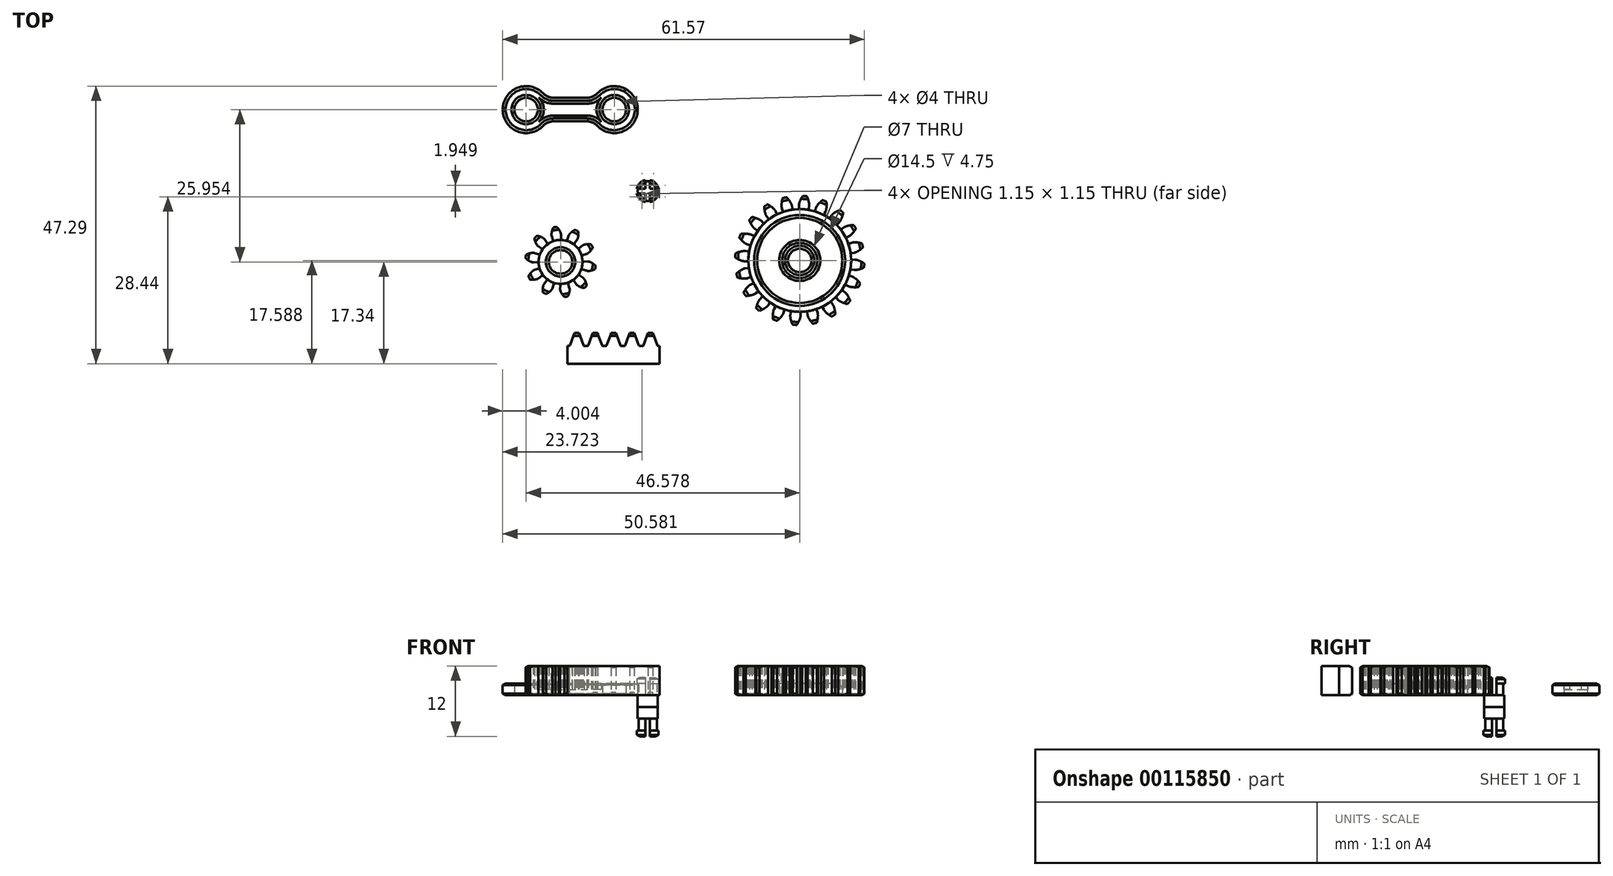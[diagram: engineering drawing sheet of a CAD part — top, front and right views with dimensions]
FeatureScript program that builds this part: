
annotation { "Feature Type Name" : "Feature", "Feature Type Description" : "" }
export const myFeature = defineFeature(function(context is Context, id is Id, definition is map)
    precondition{}
    {
        {
            var Q0;
            Q0=qCreatedBy(makeId("Top.planeOp"),FACE);
            var sketch = newSketch(context, id + "F0", { "sketchPlane" : qUnion([Q0])});
            skArc(sketch, "E0", {"start": v(4.77, -1.23) * mm, "mid": v(4.82, -0.94) * mm, "end": v(4.86, -0.65) * mm});
            skFitSpline(sketch, "E1", {"points": [v(3.6, 0.07) * mm, v(3.6, 0.07) * mm, v(3.6, 0.07) * mm, v(3.6, 0.07) * mm, v(3.6, 0.07) * mm, v(3.6, 0.07) * mm, v(3.6, 0.07) * mm, v(3.62, 0.07) * mm, v(3.63, 0.07) * mm, v(3.64, 0.07) * mm, v(3.65, 0.06) * mm, v(3.66, 0.06) * mm, v(3.68, 0.06) * mm, v(3.7, 0.06) * mm, v(3.71, 0.05) * mm, v(3.73, 0.05) * mm, v(3.75, 0.04) * mm, v(3.77, 0.04) * mm, v(3.8, 0.03) * mm, v(3.82, 0.03) * mm, v(3.84, 0.02) * mm, v(3.87, 0) * mm, v(3.9, 0) * mm, v(3.93, -0.01) * mm, v(3.96, -0.02) * mm, v(3.99, -0.04) * mm, v(4.02, -0.05) * mm, v(4.05, -0.07) * mm, v(4.09, -0.08) * mm, v(4.12, -0.1) * mm, v(4.16, -0.12) * mm, v(4.2, -0.14) * mm, v(4.23, -0.16) * mm, v(4.27, -0.18) * mm, v(4.31, -0.2) * mm, v(4.35, -0.23) * mm, v(4.4, -0.26) * mm, v(4.43, -0.3) * mm, v(4.48, -0.32) * mm, v(4.52, -0.35) * mm, v(4.56, -0.39) * mm, v(4.6, -0.42) * mm, v(4.65, -0.46) * mm, v(4.7, -0.5) * mm, v(4.74, -0.54) * mm, v(4.79, -0.58) * mm, v(4.83, -0.62) * mm, v(4.85, -0.64) * mm, v(4.86, -0.65) * mm]});
            skFitSpline(sketch, "E2", {"points": [v(3.34, -1.52) * mm, v(3.34, -1.52) * mm, v(3.34, -1.52) * mm, v(3.34, -1.52) * mm, v(3.35, -1.52) * mm, v(3.35, -1.52) * mm, v(3.36, -1.52) * mm, v(3.36, -1.53) * mm, v(3.37, -1.53) * mm, v(3.38, -1.53) * mm, v(3.4, -1.53) * mm, v(3.4, -1.53) * mm, v(3.42, -1.54) * mm, v(3.44, -1.54) * mm, v(3.46, -1.54) * mm, v(3.48, -1.54) * mm, v(3.5, -1.54) * mm, v(3.52, -1.54) * mm, v(3.54, -1.55) * mm, v(3.57, -1.55) * mm, v(3.6, -1.55) * mm, v(3.62, -1.55) * mm, v(3.65, -1.54) * mm, v(3.68, -1.54) * mm, v(3.72, -1.54) * mm, v(3.75, -1.54) * mm, v(3.78, -1.54) * mm, v(3.82, -1.53) * mm, v(3.86, -1.53) * mm, v(3.9, -1.52) * mm, v(3.94, -1.51) * mm, v(3.98, -1.5) * mm, v(4.02, -1.5) * mm, v(4.07, -1.49) * mm, v(4.11, -1.48) * mm, v(4.16, -1.46) * mm, v(4.2, -1.45) * mm, v(4.25, -1.44) * mm, v(4.3, -1.42) * mm, v(4.35, -1.4) * mm, v(4.4, -1.38) * mm, v(4.46, -1.36) * mm, v(4.51, -1.34) * mm, v(4.57, -1.32) * mm, v(4.62, -1.3) * mm, v(4.68, -1.27) * mm, v(4.73, -1.25) * mm, v(4.76, -1.23) * mm, v(4.77, -1.23) * mm]});
            skLineSegment(sketch, "E3", {"start": v(3.6, 0.07) * mm, "end": v(2.88, 0.06) * mm});
            skLineSegment(sketch, "E4", {"start": v(2.67, -1.3) * mm, "end": v(3.34, -1.52) * mm});
            skArc(sketch, "E5", {"start": v(2.36, -1.43) * mm, "mid": v(-4.81, 0.59) * mm, "end": v(2.63, 0.3) * mm});
            skPoint(sketch, "E6.visualSharp", {"position": v(2.64, 0.06) * mm});
            skArc(sketch, "E6.filletArc", {"start": v(2.63, 0.3) * mm, "mid": v(2.71, 0.12) * mm, "end": v(2.88, 0.06) * mm});
            skPoint(sketch, "E7.visualSharp", {"position": v(2.44, -1.21) * mm});
            skArc(sketch, "E7.filletArc", {"start": v(2.67, -1.3) * mm, "mid": v(2.49, -1.3) * mm, "end": v(2.36, -1.43) * mm});
            skCircle(sketch, "E8", {"center": v(-1.1, 0) * mm, "radius": 2 * mm});
            skCircle(sketch, "E9", {"center": v(-1.1, 0) * mm, "radius": 3.75 * mm});
            skSolve(sketch);
        }
        {
            var Q0;
            Q0=makeQuery(id+"F0.imprint","IMPRINT",FACE,{"disambiguationData":[TD([[makeQuery(id+"F0.imprint","IMPRINT",EDGE,{"derivedFrom":sQuery(id+"F0.wireOp",EDGE,"E0")}),1.0]])]});
            extrude(context, id + "F1", {"entities" : qUnion([Q0]), "depth" : 5 * mm});
        }
        {
            var Q0;
            Q0=makeQuery(id+"F1.opExtrude","CAP_EDGE",EDGE,{"disambiguationData":[OSD([sQuery(id+"F0.wireOp",EDGE,"E0")])],"isStart":false});
            var Q1;
            Q1=makeQuery(id+"F1.opExtrude","CAP_EDGE",EDGE,{"disambiguationData":[OSD([sQuery(id+"F0.wireOp",EDGE,"E0")])],"isStart":true});
            chamfer(context, id + "F2", {"entities" : qUnion([Q0, Q1]), "chamferType" : ChamferType.TWO_OFFSETS, "width1" : .5 * mm, "oppositeDirection" : false, "width2" : .25 * mm, "tangentPropagation" : true});
        }
        {
            var Q0;
            Q0=makeQuery(id+"F1.opExtrude","SWEPT_BODY",BODY,{"disambiguationData":[OSD([sQuery(id+"F0.wireOp",EDGE,"E0"),sQuery(id+"F0.wireOp",EDGE,"E1"),sQuery(id+"F0.wireOp",EDGE,"E2"),sQuery(id+"F0.wireOp",EDGE,"E3"),sQuery(id+"F0.wireOp",EDGE,"E4"),sQuery(id+"F0.wireOp",EDGE,"E6.filletArc"),sQuery(id+"F0.wireOp",EDGE,"E7.filletArc"),sQuery(id+"F0.wireOp",EDGE,"E9")])]});
            var Q1;
            Q1=sQuery(id+"F0.wireOp",EDGE,"E8");
            circularPattern(context, id + "F3", {"entities" : qUnion([Q0]), "axis" : qUnion([Q1]), "angle" : 36 * degree, "instanceCount" : 10});
        }
        {
            var Q0;
            Q0=makeQuery(id+"F0.imprint","IMPRINT",FACE,{"disambiguationData":[TD([[makeQuery(id+"F0.imprint","IMPRINT",EDGE,{"derivedFrom":sQuery(id+"F0.wireOp",EDGE,"E8")}),-1.0]])]});
            extrude(context, id + "F4", {"entities" : qUnion([Q0]), "depth" : 5 * mm});
        }
        {
            var Q0;
            Q0=makeQuery(id+"F4.opExtrude","CAP_EDGE",EDGE,{"disambiguationData":[OSD([sQuery(id+"F0.wireOp",EDGE,"E8")])],"isStart":false});
            var Q1;
            Q1=makeQuery(id+"F4.opExtrude","CAP_EDGE",EDGE,{"disambiguationData":[OSD([sQuery(id+"F0.wireOp",EDGE,"E8")])],"isStart":true});
            chamfer(context, id + "F5", {"entities" : qUnion([Q0, Q1]), "chamferType" : ChamferType.TWO_OFFSETS, "width1" : .25 * mm, "oppositeDirection" : false, "width2" : .5 * mm, "tangentPropagation" : true});
        }
        {
            var Q0;
            Q0=qCreatedBy(makeId("Top.planeOp"),FACE);
            var sketch = newSketch(context, id + "F6", { "sketchPlane" : qUnion([Q0])});
            skArc(sketch, "E10", {"start": v(50.54, -0.96) * mm, "mid": v(50.58, -0.62) * mm, "end": v(50.6, -0.27) * mm});
            skFitSpline(sketch, "E11", {"points": [v(49, 0.39) * mm, v(49, 0.39) * mm, v(49, 0.39) * mm, v(49.01, 0.39) * mm, v(49.02, 0.39) * mm, v(49.03, 0.39) * mm, v(49.04, 0.39) * mm, v(49.06, 0.39) * mm, v(49.08, 0.38) * mm, v(49.1, 0.38) * mm, v(49.12, 0.38) * mm, v(49.15, 0.37) * mm, v(49.18, 0.37) * mm, v(49.21, 0.36) * mm, v(49.25, 0.36) * mm, v(49.29, 0.35) * mm, v(49.33, 0.34) * mm, v(49.37, 0.33) * mm, v(49.41, 0.31) * mm, v(49.46, 0.3) * mm, v(49.51, 0.28) * mm, v(49.57, 0.26) * mm, v(49.62, 0.24) * mm, v(49.68, 0.22) * mm, v(49.74, 0.2) * mm, v(49.8, 0.17) * mm, v(49.86, 0.15) * mm, v(49.93, 0.11) * mm, v(50, 0.08) * mm, v(50.07, 0.05) * mm, v(50.14, 0) * mm, v(50.22, -0.03) * mm, v(50.3, -0.07) * mm, v(50.37, -0.12) * mm, v(50.45, -0.17) * mm, v(50.53, -0.22) * mm, v(50.58, -0.25) * mm, v(50.6, -0.27) * mm]});
            skFitSpline(sketch, "E12", {"points": [v(48.87, -1.36) * mm, v(48.87, -1.36) * mm, v(48.87, -1.36) * mm, v(48.88, -1.36) * mm, v(48.88, -1.36) * mm, v(48.9, -1.36) * mm, v(48.9, -1.36) * mm, v(48.92, -1.37) * mm, v(48.94, -1.37) * mm, v(48.96, -1.37) * mm, v(48.99, -1.37) * mm, v(49.01, -1.37) * mm, v(49.04, -1.37) * mm, v(49.08, -1.37) * mm, v(49.11, -1.37) * mm, v(49.15, -1.36) * mm, v(49.2, -1.36) * mm, v(49.24, -1.36) * mm, v(49.28, -1.35) * mm, v(49.33, -1.34) * mm, v(49.39, -1.33) * mm, v(49.44, -1.33) * mm, v(49.5, -1.31) * mm, v(49.56, -1.3) * mm, v(49.62, -1.29) * mm, v(49.69, -1.27) * mm, v(49.75, -1.25) * mm, v(49.82, -1.23) * mm, v(49.9, -1.21) * mm, v(49.97, -1.19) * mm, v(50.05, -1.16) * mm, v(50.13, -1.13) * mm, v(50.21, -1.1) * mm, v(50.3, -1.07) * mm, v(50.38, -1.03) * mm, v(50.46, -1) * mm, v(50.52, -0.97) * mm, v(50.54, -0.96) * mm]});
            skLineSegment(sketch, "E13", {"start": v(49, 0.39) * mm, "end": v(48.6, 0.38) * mm});
            skLineSegment(sketch, "E14", {"start": v(48.48, -1.3) * mm, "end": v(48.87, -1.36) * mm});
            skArc(sketch, "E15", {"start": v(48.19, -1.49) * mm, "mid": v(30.89, 0.93) * mm, "end": v(48.35, 0.62) * mm});
            skPoint(sketch, "E16.visualSharp", {"position": v(48.36, 0.38) * mm});
            skArc(sketch, "E16.filletArc", {"start": v(48.35, 0.62) * mm, "mid": v(48.43, 0.45) * mm, "end": v(48.6, 0.38) * mm});
            skPoint(sketch, "E17.visualSharp", {"position": v(48.23, -1.25) * mm});
            skArc(sketch, "E17.filletArc", {"start": v(48.48, -1.3) * mm, "mid": v(48.3, -1.33) * mm, "end": v(48.19, -1.49) * mm});
            skCircle(sketch, "E18", {"center": v(39.61, 0.25) * mm, "radius": 8.75 * mm});
            skCircle(sketch, "E19", {"center": v(39.61, 0.25) * mm, "radius": 2 * mm});
            skCircle(sketch, "E20", {"center": v(39.61, 0.25) * mm, "radius": 3.5 * mm});
            skCircle(sketch, "E21", {"center": v(39.61, 0.25) * mm, "radius": 7.25 * mm});
            skSolve(sketch);
        }
        {
            var Q0;
            Q0=makeQuery(id+"F6.imprint","IMPRINT",FACE,{"disambiguationData":[TD([[makeQuery(id+"F6.imprint","IMPRINT",EDGE,{"derivedFrom":sQuery(id+"F6.wireOp",EDGE,"E10")}),1.0]])]});
            extrude(context, id + "F7", {"entities" : qUnion([Q0]), "depth" : 5 * mm});
        }
        {
            var Q0;
            Q0=makeQuery(id+"F7.opExtrude","CAP_EDGE",EDGE,{"disambiguationData":[OSD([sQuery(id+"F6.wireOp",EDGE,"E10")])],"isStart":false});
            var Q1;
            Q1=makeQuery(id+"F7.opExtrude","CAP_EDGE",EDGE,{"disambiguationData":[OSD([sQuery(id+"F6.wireOp",EDGE,"E10")])],"isStart":true});
            chamfer(context, id + "F8", {"entities" : qUnion([Q0, Q1]), "chamferType" : ChamferType.TWO_OFFSETS, "width1" : .5 * mm, "oppositeDirection" : false, "width2" : .25 * mm, "tangentPropagation" : true});
        }
        {
            var Q0;
            Q0=makeQuery(id+"F7.opExtrude","SWEPT_BODY",BODY,{"disambiguationData":[OSD([sQuery(id+"F6.wireOp",EDGE,"E10"),sQuery(id+"F6.wireOp",EDGE,"E11"),sQuery(id+"F6.wireOp",EDGE,"E12"),sQuery(id+"F6.wireOp",EDGE,"E13"),sQuery(id+"F6.wireOp",EDGE,"E14"),sQuery(id+"F6.wireOp",EDGE,"E16.filletArc"),sQuery(id+"F6.wireOp",EDGE,"E17.filletArc"),sQuery(id+"F6.wireOp",EDGE,"E18")])]});
            var Q1;
            Q1=sQuery(id+"F6.wireOp",EDGE,"E19");
            circularPattern(context, id + "F9", {"entities" : qUnion([Q0]), "axis" : qUnion([Q1]), "angle" : 18 * degree, "instanceCount" : 20});
        }
        {
            var Q0;
            Q0=makeQuery(id+"F6.imprint","IMPRINT",FACE,{"disambiguationData":[TD([[makeQuery(id+"F6.imprint","IMPRINT",EDGE,{"derivedFrom":sQuery(id+"F6.wireOp",EDGE,"E21")}),-1.0]])]});
            var Q1;
            Q1=makeQuery(id+"F6.imprint","IMPRINT",FACE,{"disambiguationData":[TD([[makeQuery(id+"F6.imprint","IMPRINT",EDGE,{"derivedFrom":sQuery(id+"F6.wireOp",EDGE,"E19")}),-1.0]])]});
            extrude(context, id + "F10", {"entities" : qUnion([Q0, Q1]), "depth" : 5 * mm});
        }
        {
            var Q0;
            Q0=makeQuery(id+"F6.imprint","IMPRINT",FACE,{"disambiguationData":[TD([[makeQuery(id+"F6.imprint","IMPRINT",EDGE,{"derivedFrom":sQuery(id+"F6.wireOp",EDGE,"E20")}),-1.0]])]});
            extrude(context, id + "F11", {"entities" : qUnion([Q0]), "depth" : 2 * mm});
        }
        {
            var Q0;
            Q0=makeQuery(id+"F11.opExtrude","CAP_EDGE",EDGE,{"disambiguationData":[OSD([sQuery(id+"F6.wireOp",EDGE,"E21")])],"isStart":false});
            var Q1;
            Q1=makeQuery(id+"F11.opExtrude","CAP_EDGE",EDGE,{"disambiguationData":[OSD([sQuery(id+"F6.wireOp",EDGE,"E20")])],"isStart":false});
            fillet(context, id + "F12", {"entities" : qUnion([Q0, Q1]), "radius" : 1 * mm, "tangentPropagation" : true, "allowEdgeOverflow" : false});
        }
        {
            var Q0;
            Q0=makeQuery(id+"F10.opExtrude","CAP_EDGE",EDGE,{"disambiguationData":[OSD([sQuery(id+"F6.wireOp",EDGE,"E21")])],"isStart":false});
            var Q1;
            Q1=makeQuery(id+"F10.opExtrude","CAP_EDGE",EDGE,{"disambiguationData":[OSD([sQuery(id+"F6.wireOp",EDGE,"E19")])],"isStart":false});
            chamfer(context, id + "F13", {"entities" : qUnion([Q0, Q1]), "chamferType" : ChamferType.TWO_OFFSETS, "width1" : .25 * mm, "oppositeDirection" : false, "width2" : .5 * mm, "tangentPropagation" : true});
        }
        {
            var Q0;
            Q0=makeQuery(id+"F10.opExtrude","CAP_EDGE",EDGE,{"disambiguationData":[OSD([sQuery(id+"F6.wireOp",EDGE,"E20")])],"isStart":false});
            var Q1;
            Q1=makeQuery(id+"F10.opExtrude","CAP_EDGE",EDGE,{"disambiguationData":[OSD([sQuery(id+"F6.wireOp",EDGE,"E19")])],"isStart":true});
            chamfer(context, id + "F14", {"entities" : qUnion([Q0, Q1]), "chamferType" : ChamferType.TWO_OFFSETS, "width1" : .5 * mm, "oppositeDirection" : false, "width2" : .25 * mm, "tangentPropagation" : true});
        }
        {
            var Q0;
            Q0=qCreatedBy(makeId("Top.planeOp"),FACE);
            var sketch = newSketch(context, id + "F15", { "sketchPlane" : qUnion([Q0])});
            skLineSegment(sketch, "E22", {"start": v(0.48, -14.18) * mm, "end": v(1.24, -12.1) * mm});
            skLineSegment(sketch, "E23", {"start": v(1.24, -12.1) * mm, "end": v(2.04, -12.1) * mm});
            skLineSegment(sketch, "E24", {"start": v(2.04, -12.1) * mm, "end": v(2.8, -14.18) * mm});
            skLineSegment(sketch, "E25", {"start": v(3.03, -14.34) * mm, "end": v(3.38, -14.34) * mm});
            skLineSegment(sketch, "E26", {"start": v(3.62, -14.18) * mm, "end": v(4.38, -12.1) * mm});
            skLineSegment(sketch, "E27", {"start": v(4.38, -12.1) * mm, "end": v(5.18, -12.1) * mm});
            skLineSegment(sketch, "E28", {"start": v(5.18, -12.1) * mm, "end": v(5.94, -14.18) * mm});
            skLineSegment(sketch, "E29", {"start": v(6.17, -14.34) * mm, "end": v(6.53, -14.34) * mm});
            skLineSegment(sketch, "E30", {"start": v(6.76, -14.18) * mm, "end": v(7.52, -12.1) * mm});
            skLineSegment(sketch, "E31", {"start": v(7.52, -12.1) * mm, "end": v(8.32, -12.1) * mm});
            skLineSegment(sketch, "E32", {"start": v(8.32, -12.1) * mm, "end": v(9.08, -14.18) * mm});
            skLineSegment(sketch, "E33", {"start": v(9.31, -14.34) * mm, "end": v(9.67, -14.34) * mm});
            skLineSegment(sketch, "E34", {"start": v(9.9, -14.18) * mm, "end": v(10.66, -12.1) * mm});
            skLineSegment(sketch, "E35", {"start": v(10.66, -12.1) * mm, "end": v(11.46, -12.1) * mm});
            skLineSegment(sketch, "E36", {"start": v(11.46, -12.1) * mm, "end": v(12.22, -14.18) * mm});
            skLineSegment(sketch, "E37", {"start": v(12.46, -14.34) * mm, "end": v(12.8, -14.34) * mm});
            skLineSegment(sketch, "E38", {"start": v(13.04, -14.18) * mm, "end": v(13.8, -12.1) * mm});
            skLineSegment(sketch, "E39", {"start": v(13.8, -12.1) * mm, "end": v(14.6, -12.1) * mm});
            skLineSegment(sketch, "E40", {"start": v(14.6, -12.1) * mm, "end": v(15.36, -14.18) * mm});
            skLineSegment(sketch, "E41", {"start": v(0.07, -14.34) * mm, "end": v(0.07, -17.34) * mm});
            skLineSegment(sketch, "E42", {"start": v(15.77, -14.34) * mm, "end": v(15.77, -17.34) * mm});
            skLineSegment(sketch, "E43", {"start": v(0.07, -14.34) * mm, "end": v(0.24, -14.34) * mm});
            skLineSegment(sketch, "E44", {"start": v(0.07, -17.34) * mm, "end": v(15.77, -17.34) * mm});
            skLineSegment(sketch, "E45", {"start": v(15.6, -14.34) * mm, "end": v(15.77, -14.34) * mm});
            skPoint(sketch, "E46.visualSharp", {"position": v(0.42, -14.34) * mm});
            skArc(sketch, "E46.filletArc", {"start": v(0.24, -14.34) * mm, "mid": v(0.39, -14.3) * mm, "end": v(0.48, -14.18) * mm});
            skPoint(sketch, "E47.visualSharp", {"position": v(2.86, -14.34) * mm});
            skArc(sketch, "E47.filletArc", {"start": v(2.8, -14.18) * mm, "mid": v(2.89, -14.3) * mm, "end": v(3.03, -14.34) * mm});
            skPoint(sketch, "E48.visualSharp", {"position": v(3.56, -14.34) * mm});
            skArc(sketch, "E48.filletArc", {"start": v(3.38, -14.34) * mm, "mid": v(3.53, -14.3) * mm, "end": v(3.62, -14.18) * mm});
            skPoint(sketch, "E49.visualSharp", {"position": v(6, -14.34) * mm});
            skArc(sketch, "E49.filletArc", {"start": v(5.94, -14.18) * mm, "mid": v(6.03, -14.3) * mm, "end": v(6.17, -14.34) * mm});
            skPoint(sketch, "E50.visualSharp", {"position": v(6.7, -14.34) * mm});
            skArc(sketch, "E50.filletArc", {"start": v(6.53, -14.34) * mm, "mid": v(6.67, -14.3) * mm, "end": v(6.76, -14.18) * mm});
            skPoint(sketch, "E51.visualSharp", {"position": v(9.14, -14.34) * mm});
            skArc(sketch, "E51.filletArc", {"start": v(9.08, -14.18) * mm, "mid": v(9.17, -14.3) * mm, "end": v(9.31, -14.34) * mm});
            skPoint(sketch, "E52.visualSharp", {"position": v(9.84, -14.34) * mm});
            skArc(sketch, "E52.filletArc", {"start": v(9.67, -14.34) * mm, "mid": v(9.81, -14.3) * mm, "end": v(9.9, -14.18) * mm});
            skPoint(sketch, "E53.visualSharp", {"position": v(12.28, -14.34) * mm});
            skArc(sketch, "E53.filletArc", {"start": v(12.22, -14.18) * mm, "mid": v(12.31, -14.3) * mm, "end": v(12.46, -14.34) * mm});
            skPoint(sketch, "E54.visualSharp", {"position": v(12.98, -14.34) * mm});
            skArc(sketch, "E54.filletArc", {"start": v(12.8, -14.34) * mm, "mid": v(12.95, -14.3) * mm, "end": v(13.04, -14.18) * mm});
            skPoint(sketch, "E55.visualSharp", {"position": v(15.42, -14.34) * mm});
            skArc(sketch, "E55.filletArc", {"start": v(15.36, -14.18) * mm, "mid": v(15.45, -14.3) * mm, "end": v(15.6, -14.34) * mm});
            skSolve(sketch);
        }
        {
            var Q0;
            Q0=makeQuery(id+"F15.imprint","IMPRINT",FACE,{"disambiguationData":[TD([[makeQuery(id+"F15.imprint","IMPRINT",EDGE,{"derivedFrom":sQuery(id+"F15.wireOp",EDGE,"E22")}),-1.0]])]});
            extrude(context, id + "F16", {"entities" : qUnion([Q0]), "depth" : 5 * mm});
        }
        {
            var Q0;
            Q0=makeQuery(id+"F16.opExtrude","CAP_EDGE",EDGE,{"disambiguationData":[OSD([sQuery(id+"F15.wireOp",EDGE,"E23")])],"isStart":false});
            var Q1;
            Q1=makeQuery(id+"F16.opExtrude","CAP_EDGE",EDGE,{"disambiguationData":[OSD([sQuery(id+"F15.wireOp",EDGE,"E27")])],"isStart":false});
            var Q2;
            Q2=makeQuery(id+"F16.opExtrude","CAP_EDGE",EDGE,{"disambiguationData":[OSD([sQuery(id+"F15.wireOp",EDGE,"E31")])],"isStart":false});
            var Q3;
            Q3=makeQuery(id+"F16.opExtrude","CAP_EDGE",EDGE,{"disambiguationData":[OSD([sQuery(id+"F15.wireOp",EDGE,"E35")])],"isStart":false});
            var Q4;
            Q4=makeQuery(id+"F16.opExtrude","CAP_EDGE",EDGE,{"disambiguationData":[OSD([sQuery(id+"F15.wireOp",EDGE,"E39")])],"isStart":false});
            var Q5;
            Q5=makeQuery(id+"F16.opExtrude","CAP_EDGE",EDGE,{"disambiguationData":[OSD([sQuery(id+"F15.wireOp",EDGE,"E39")])],"isStart":true});
            var Q6;
            Q6=makeQuery(id+"F16.opExtrude","CAP_EDGE",EDGE,{"disambiguationData":[OSD([sQuery(id+"F15.wireOp",EDGE,"E35")])],"isStart":true});
            var Q7;
            Q7=makeQuery(id+"F16.opExtrude","CAP_EDGE",EDGE,{"disambiguationData":[OSD([sQuery(id+"F15.wireOp",EDGE,"E31")])],"isStart":true});
            var Q8;
            Q8=makeQuery(id+"F16.opExtrude","CAP_EDGE",EDGE,{"disambiguationData":[OSD([sQuery(id+"F15.wireOp",EDGE,"E27")])],"isStart":true});
            var Q9;
            Q9=makeQuery(id+"F16.opExtrude","CAP_EDGE",EDGE,{"disambiguationData":[OSD([sQuery(id+"F15.wireOp",EDGE,"E23")])],"isStart":true});
            chamfer(context, id + "F17", {"entities" : qUnion([Q0, Q1, Q2, Q3, Q4, Q5, Q6, Q7, Q8, Q9]), "chamferType" : ChamferType.TWO_OFFSETS, "width1" : .25 * mm, "oppositeDirection" : false, "width2" : .5 * mm, "tangentPropagation" : true});
        }
        {
            var Q0;
            Q0=qCreatedBy(makeId("Top.planeOp"),FACE);
            var sketch = newSketch(context, id + "F18", { "sketchPlane" : qUnion([Q0])});
            skLineSegment(sketch, "E56", {"start": v(-6.97, 25.95) * mm, "end": v(8.03, 25.95) * mm, "construction": true});
            skCircle(sketch, "E57", {"center": v(-6.97, 25.95) * mm, "radius": 2 * mm});
            skCircle(sketch, "E58", {"center": v(8.03, 25.95) * mm, "radius": 2 * mm});
            skArc(sketch, "E59.0", {"start": v(5.15, 23.18) * mm, "mid": v(12.03, 25.95) * mm, "end": v(5.15, 28.72) * mm});
            skArc(sketch, "E60.0", {"start": v(-4.08, 28.72) * mm, "mid": v(-10.97, 25.95) * mm, "end": v(-4.08, 23.18) * mm});
            skLineSegment(sketch, "E61.0", {"start": v(-2.28, 23.95) * mm, "end": v(3.34, 23.95) * mm});
            skLineSegment(sketch, "E62.0", {"start": v(-2.28, 27.95) * mm, "end": v(3.34, 27.95) * mm});
            skPoint(sketch, "E63.visualSharp", {"position": v(-3.5, 27.95) * mm});
            skArc(sketch, "E63.filletArc", {"start": v(-4.08, 28.72) * mm, "mid": v(-3.26, 28.15) * mm, "end": v(-2.28, 27.95) * mm});
            skPoint(sketch, "E64.visualSharp", {"position": v(-3.5, 23.95) * mm});
            skArc(sketch, "E64.filletArc", {"start": v(-2.28, 23.95) * mm, "mid": v(-3.26, 23.75) * mm, "end": v(-4.08, 23.18) * mm});
            skPoint(sketch, "E65.visualSharp", {"position": v(4.57, 23.95) * mm});
            skArc(sketch, "E65.filletArc", {"start": v(5.15, 23.18) * mm, "mid": v(4.32, 23.75) * mm, "end": v(3.34, 23.95) * mm});
            skPoint(sketch, "E66.visualSharp", {"position": v(4.57, 27.95) * mm});
            skArc(sketch, "E66.filletArc", {"start": v(3.34, 27.95) * mm, "mid": v(4.32, 28.15) * mm, "end": v(5.15, 28.72) * mm});
            skSolve(sketch);
        }
        {
            var Q0;
            Q0=makeQuery(id+"F18.imprint","IMPRINT",FACE,{"disambiguationData":[TD([[makeQuery(id+"F18.imprint","IMPRINT",EDGE,{"derivedFrom":sQuery(id+"F18.wireOp",EDGE,"E57")}),-1.0]])]});
            extrude(context, id + "F19", {"entities" : qUnion([Q0]), "depth" : 2 * mm});
        }
        {
            var Q0;
            Q0=makeQuery(id+"F19.opExtrude","CAP_FACE",FACE,{"disambiguationData":[OSD([sQuery(id+"F18.wireOp",EDGE,"E57"),sQuery(id+"F18.wireOp",EDGE,"E58"),sQuery(id+"F18.wireOp",EDGE,"E59.0"),sQuery(id+"F18.wireOp",EDGE,"E60.0"),sQuery(id+"F18.wireOp",EDGE,"E61.0"),sQuery(id+"F18.wireOp",EDGE,"E62.0"),sQuery(id+"F18.wireOp",EDGE,"E63.filletArc"),sQuery(id+"F18.wireOp",EDGE,"E64.filletArc"),sQuery(id+"F18.wireOp",EDGE,"E65.filletArc"),sQuery(id+"F18.wireOp",EDGE,"E66.filletArc")])],"isStart":false});
            shell(context, id + "F20", {"entities" : qUnion([Q0]), "thickness" : 1 * mm});
        }
        {
            var Q0;
            Q0=makeQuery(id+"F19.opExtrude","CAP_EDGE",EDGE,{"disambiguationData":[OSD([sQuery(id+"F18.wireOp",EDGE,"E61.0")])],"isStart":false});
            var Q1;
            Q1=makeQuery(id+"F19.opExtrude","CAP_EDGE",EDGE,{"disambiguationData":[OSD([sQuery(id+"F18.wireOp",EDGE,"E61.0")])],"isStart":true});
            chamfer(context, id + "F21", {"entities" : qUnion([Q0, Q1]), "chamferType" : ChamferType.TWO_OFFSETS, "width1" : .25 * mm, "oppositeDirection" : true, "width2" : .5 * mm, "tangentPropagation" : true});
        }
        {
            var Q0;
            Q0=makeQuery(id+"F19.opExtrude","CAP_EDGE",EDGE,{"disambiguationData":[OSD([sQuery(id+"F18.wireOp",EDGE,"E57")])],"isStart":false});
            var Q1;
            Q1=makeQuery(id+"F19.opExtrude","CAP_EDGE",EDGE,{"disambiguationData":[OSD([sQuery(id+"F18.wireOp",EDGE,"E58")])],"isStart":false});
            chamfer(context, id + "F22", {"entities" : qUnion([Q0, Q1]), "chamferType" : ChamferType.TWO_OFFSETS, "width1" : .25 * mm, "oppositeDirection" : false, "width2" : .5 * mm, "tangentPropagation" : true});
        }
        {
            var Q0;
            Q0=makeQuery(id+"F19.opExtrude","CAP_EDGE",EDGE,{"disambiguationData":[OSD([sQuery(id+"F18.wireOp",EDGE,"E58")])],"isStart":true});
            var Q1;
            Q1=makeQuery(id+"F19.opExtrude","CAP_EDGE",EDGE,{"disambiguationData":[OSD([sQuery(id+"F18.wireOp",EDGE,"E57")])],"isStart":true});
            chamfer(context, id + "F23", {"entities" : qUnion([Q0, Q1]), "chamferType" : ChamferType.TWO_OFFSETS, "width1" : .25 * mm, "oppositeDirection" : true, "width2" : .5 * mm, "tangentPropagation" : true});
        }
        {
            var Q0;
            Q0=qCreatedBy(makeId("Top.planeOp"),FACE);
            var sketch = newSketch(context, id + "F24", { "sketchPlane" : qUnion([Q0])});
            skArc(sketch, "E67", {"start": v(13.33, 13.62) * mm, "mid": v(12.6, 13.2) * mm, "end": v(12.18, 12.47) * mm});
            skArc(sketch, "E68", {"start": v(13.73, 13.77) * mm, "mid": v(12.53, 13.28) * mm, "end": v(12.03, 12.07) * mm});
            skLineSegment(sketch, "E69", {"start": v(13.73, 12.07) * mm, "end": v(13.73, 13.77) * mm});
            skLineSegment(sketch, "E70", {"start": v(13.73, 12.07) * mm, "end": v(12.03, 12.07) * mm});
            skLineSegment(sketch, "E71.0", {"start": v(13.33, 12.47) * mm, "end": v(13.33, 13.62) * mm});
            skLineSegment(sketch, "E72.0", {"start": v(13.33, 12.47) * mm, "end": v(12.18, 12.47) * mm});
            skLineSegment(sketch, "E73.trimOffspring", {"start": v(13.33, 13.73) * mm, "end": v(13.33, 15.07) * mm});
            skLineSegment(sketch, "E74.trimOffspring", {"start": v(12.08, 12.47) * mm, "end": v(10.73, 12.47) * mm});
            skArc(sketch, "E75", {"start": v(13.73, 13.97) * mm, "mid": v(12.38, 13.42) * mm, "end": v(11.83, 12.07) * mm});
            skSolve(sketch);
        }
        {
            var Q0;
            Q0=makeQuery(id+"F24.imprint","IMPRINT",FACE,{"disambiguationData":[TD([[makeQuery(id+"F24.imprint","IMPRINT",EDGE,{"derivedFrom":sQuery(id+"F24.wireOp",EDGE,"E67")}),1.0]])]});
            extrude(context, id + "F25", {"entities" : qUnion([Q0]), "depth" : 2 * mm});
        }
        {
            var Q0;
            Q0=makeQuery(id+"F24.imprint","IMPRINT",FACE,{"disambiguationData":[TD([[makeQuery(id+"F24.imprint","IMPRINT",EDGE,{"derivedFrom":sQuery(id+"F24.wireOp",EDGE,"E67")}),-1.0]])]});
            var Q1;
            {var subQ5=sQuery(id+"F24.wireOp",EDGE,"E75");Q1=makeQuery(id+"F24.imprint","IMPRINT",FACE,{"disambiguationData":[TD([[makeQuery(id+"F24.imprint","IMPRINT",EDGE,{"derivedFrom":subQ5}),-1.0]])]});}
            var Q2;
            Q2=makeQuery(id+"F24.imprint","IMPRINT",FACE,{"disambiguationData":[TD([[makeQuery(id+"F24.imprint","IMPRINT",EDGE,{"derivedFrom":sQuery(id+"F24.wireOp",EDGE,"E67")}),1.0]])]});
            extrude(context, id + "F26", {"entities" : qUnion([Q0, Q1, Q2]), "operationType" : NewBodyOperationType.ADD, "oppositeDirection" : true, "depth" : 2 * mm});
        }
        {
            var Q0;
            Q0=makeQuery(id+"F25.opExtrude","CAP_FACE",FACE,{"disambiguationData":[OSD([sQuery(id+"F24.wireOp",EDGE,"E67"),sQuery(id+"F24.wireOp",EDGE,"E71.0"),sQuery(id+"F24.wireOp",EDGE,"E72.0")])],"isStart":false});
            var sketch = newSketch(context, id + "F27", { "sketchPlane" : qUnion([Q0])});
            skArc(sketch, "E76.0", {"start": v(13.73, 13.97) * mm, "mid": v(12.38, 13.42) * mm, "end": v(11.83, 12.07) * mm});
            skLineSegment(sketch, "E77.0", {"start": v(13.73, 12.07) * mm, "end": v(13.73, 13.77) * mm});
            skLineSegment(sketch, "E78.0", {"start": v(13.73, 12.07) * mm, "end": v(12.03, 12.07) * mm});
            skLineSegment(sketch, "E79.0", {"start": v(13.33, 12.47) * mm, "end": v(12.18, 12.47) * mm});
            skLineSegment(sketch, "E80.0", {"start": v(13.33, 12.47) * mm, "end": v(13.33, 13.62) * mm});
            skLineSegment(sketch, "E81", {"start": v(13.33, 13.62) * mm, "end": v(13.33, 13.93) * mm});
            skLineSegment(sketch, "E82", {"start": v(12.18, 12.47) * mm, "end": v(11.87, 12.47) * mm});
            skSolve(sketch);
        }
        {
            var Q0;
            {var subQ0=sQuery(id+"F27.wireOp",EDGE,"E81");Q0=makeQuery(id+"F27.imprint","IMPRINT",FACE,{"disambiguationData":[TD([[makeQuery(id+"F27.imprint","IMPRINT",EDGE,{"derivedFrom":subQ0}),1.0]])]});}
            var Q1;
            Q1=makeQuery(id+"F27.imprint","IMPRINT",FACE,{"disambiguationData":[TD([[makeQuery(id+"F27.imprint","IMPRINT",EDGE,{"derivedFrom":sQuery(id+"F27.wireOp",EDGE,"E79.0")}),-1.0]])]});
            extrude(context, id + "F28", {"entities" : qUnion([Q0, Q1]), "operationType" : NewBodyOperationType.ADD, "depth" : 1 * mm});
        }
        {
            var Q0;
            Q0=makeQuery(id+"F25.opExtrude","CAP_EDGE",EDGE,{"disambiguationData":[OSD([sQuery(id+"F24.wireOp",EDGE,"E67")])],"isStart":false});
            var Q1;
            Q1=makeQuery(id+"F28.opExtrude","CAP_EDGE",EDGE,{"disambiguationData":[OSD([sQuery(id+"F27.wireOp",EDGE,"E76.0")])],"isStart":false});
            chamfer(context, id + "F29", {"entities" : qUnion([Q0, Q1]), "chamferType" : ChamferType.TWO_OFFSETS, "width1" : .25 * mm, "oppositeDirection" : true, "width2" : .5 * mm, "tangentPropagation" : true});
        }
        {
            var Q0;
            Q0=makeQuery(id+"F25.opExtrude","SWEPT_BODY",BODY,{"disambiguationData":[OSD([sQuery(id+"F24.wireOp",EDGE,"E67"),sQuery(id+"F24.wireOp",EDGE,"E71.0"),sQuery(id+"F24.wireOp",EDGE,"E72.0")])]});
            var Q1;
            Q1=makeQuery(id+"F26.opExtrude","SWEPT_BODY",BODY,{"disambiguationData":[OSD([sQuery(id+"F24.wireOp",EDGE,"E67"),sQuery(id+"F24.wireOp",EDGE,"E68"),sQuery(id+"F24.wireOp",EDGE,"E69"),sQuery(id+"F24.wireOp",EDGE,"E70"),sQuery(id+"F24.wireOp",EDGE,"E71.0"),sQuery(id+"F24.wireOp",EDGE,"E72.0")])]});
            var Q2;
            Q2=makeQuery(id+"F26.opExtrude","SWEPT_EDGE",EDGE,{"disambiguationData":[OSD([sQuery(id+"F24.wireOp",EDGE,"E69"),sQuery(id+"F24.wireOp",EDGE,"E70")])]});
            circularPattern(context, id + "F30", {"entities" : qUnion([Q0, Q1]), "axis" : qUnion([Q2]), "angle" : 90 * degree, "instanceCount" : 4});
        }
        {
            var Q0;
            Q0=makeQuery(id+"F25.opExtrude","SWEPT_BODY",BODY,{"disambiguationData":[OSD([sQuery(id+"F24.wireOp",EDGE,"E67"),sQuery(id+"F24.wireOp",EDGE,"E71.0"),sQuery(id+"F24.wireOp",EDGE,"E72.0")])]});
            var Q1;
            Q1=makeQuery(id+"F30.opPattern","COPY",BODY,{"derivedFrom":makeQuery(id+"F25.opExtrude","SWEPT_BODY",BODY,{"disambiguationData":[OSD([sQuery(id+"F24.wireOp",EDGE,"E67"),sQuery(id+"F24.wireOp",EDGE,"E71.0"),sQuery(id+"F24.wireOp",EDGE,"E72.0")])]}),"instanceName":"1"});
            var Q2;
            Q2=makeQuery(id+"F30.opPattern","COPY",BODY,{"derivedFrom":makeQuery(id+"F25.opExtrude","SWEPT_BODY",BODY,{"disambiguationData":[OSD([sQuery(id+"F24.wireOp",EDGE,"E67"),sQuery(id+"F24.wireOp",EDGE,"E71.0"),sQuery(id+"F24.wireOp",EDGE,"E72.0")])]}),"instanceName":"2"});
            var Q3;
            Q3=makeQuery(id+"F30.opPattern","COPY",BODY,{"derivedFrom":makeQuery(id+"F25.opExtrude","SWEPT_BODY",BODY,{"disambiguationData":[OSD([sQuery(id+"F24.wireOp",EDGE,"E67"),sQuery(id+"F24.wireOp",EDGE,"E71.0"),sQuery(id+"F24.wireOp",EDGE,"E72.0")])]}),"instanceName":"3"});
            booleanBodies(context, id + "F31", {"operationType" : BooleanOperationType.UNION, "tools" : qUnion([Q0, Q1, Q2, Q3])});
        }
        {
            var Q0;
            Q0=makeQuery(id+"F25.opExtrude","SWEPT_BODY",BODY,{"disambiguationData":[OSD([sQuery(id+"F24.wireOp",EDGE,"E67"),sQuery(id+"F24.wireOp",EDGE,"E71.0"),sQuery(id+"F24.wireOp",EDGE,"E72.0")])]});
            var Q1;
            {var subQ0=makeQuery(id+"F26.opExtrude","CAP_FACE",FACE,{"disambiguationData":[OSD([sQuery(id+"F24.wireOp",EDGE,"E68"),sQuery(id+"F24.wireOp",EDGE,"E69"),sQuery(id+"F24.wireOp",EDGE,"E70")])],"isStart":false});Q1=makeQuery(id+"F31.opBoolean","MERGE",FACE,{"derivedFrom":[subQ0,makeQuery(id+"F30.opPattern","COPY",FACE,{"derivedFrom":subQ0,"instanceName":"1"}),makeQuery(id+"F30.opPattern","COPY",FACE,{"derivedFrom":subQ0,"instanceName":"2"}),makeQuery(id+"F30.opPattern","COPY",FACE,{"derivedFrom":subQ0,"instanceName":"3"})]});}
            mirror(context, id + "F32", {"operationType" : NewBodyOperationType.ADD, "entities" : qUnion([Q0]), "mirrorPlane" : qUnion([Q1])});
        }
    });
